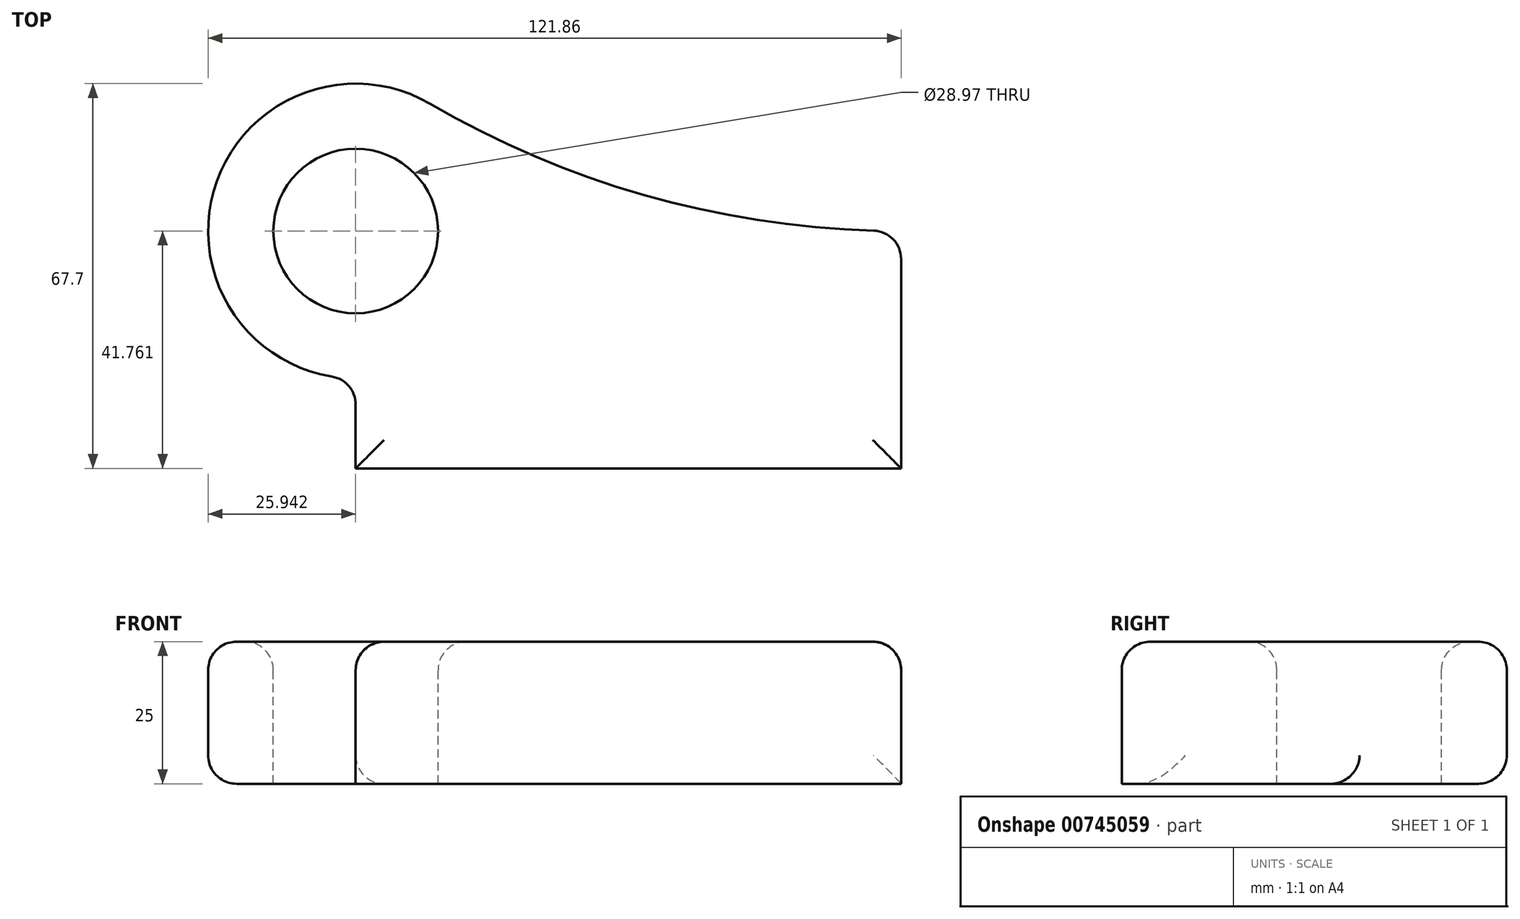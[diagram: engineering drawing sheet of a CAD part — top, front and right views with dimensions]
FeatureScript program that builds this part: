
annotation { "Feature Type Name" : "Feature", "Feature Type Description" : "" }
export const myFeature = defineFeature(function(context is Context, id is Id, definition is map)
    precondition{}
    {
        {
            var Q0;
            Q0=qCreatedBy(makeId("Top.planeOp"),FACE);
            var sketch = newSketch(context, id + "F0", { "sketchPlane" : qUnion([Q0])});
            skLineSegment(sketch, "E0.bottom", {"start": v(-47.96, -20.88) * mm, "end": v(47.96, -20.88) * mm});
            skLineSegment(sketch, "E0.top", {"start": v(-47.96, 20.88) * mm, "end": v(47.96, 20.88) * mm});
            skLineSegment(sketch, "E0.left", {"start": v(-47.96, -20.88) * mm, "end": v(-47.96, 20.88) * mm});
            skLineSegment(sketch, "E0.right", {"start": v(47.96, -20.88) * mm, "end": v(47.96, 20.88) * mm});
            skPoint(sketch, "E0.middle", {"position": v(0, 0) * mm});
            skCircle(sketch, "E1", {"center": v(-47.96, 20.88) * mm, "radius": 25.94 * mm});
            skArc(sketch, "E2", {"start": v(-34.88, 43.29) * mm, "mid": v(5.05, 26.58) * mm, "end": v(47.96, 20.88) * mm});
            skCircle(sketch, "E3", {"center": v(-47.96, 20.88) * mm, "radius": 14.48 * mm});
            skSolve(sketch);
        }
        {
            var Q0;
            {var subQ0=sQuery(id+"F0.wireOp",EDGE,"E2");Q0=makeQuery(id+"F0.imprint","IMPRINT",FACE,{"disambiguationData":[TD([[makeQuery(id+"F0.imprint","IMPRINT",EDGE,{"derivedFrom":subQ0}),-1.0]])]});}
            var Q1;
            {var subQ4=sQuery(id+"F0.wireOp",EDGE,"E0.top");var subQ6=sQuery(id+"F0.wireOp",EDGE,"E3");var subQ8=makeQuery(id+"F0.imprint","INTERSECT",VERTEX,{"derivedFrom":[subQ4,subQ6]});Q1=makeQuery(id+"F0.imprint","IMPRINT",FACE,{"disambiguationData":[TD([[makeQuery(id+"F0.imprint","IMPRINT",EDGE,{"disambiguationData":[TD([[subQ8,-1.0]])],"derivedFrom":subQ4}),1.0]])]});}
            var Q2;
            {var subQ0=sQuery(id+"F0.wireOp",EDGE,"E3");var subQ1=sQuery(id+"F0.wireOp",EDGE,"E0.top");var subQ2=makeQuery(id+"F0.imprint","INTERSECT",VERTEX,{"derivedFrom":[subQ1,subQ0]});Q2=makeQuery(id+"F0.imprint","IMPRINT",FACE,{"disambiguationData":[TD([[makeQuery(id+"F0.imprint","IMPRINT",EDGE,{"disambiguationData":[TD([[subQ2,-1.0]])],"derivedFrom":subQ1}),-1.0]])]});}
            var Q3;
            {var subQ2=sQuery(id+"F0.wireOp",EDGE,"E0.bottom");Q3=makeQuery(id+"F0.imprint","IMPRINT",FACE,{"disambiguationData":[TD([[makeQuery(id+"F0.imprint","IMPRINT",EDGE,{"derivedFrom":subQ2}),1.0]])]});}
            extrude(context, id + "F1", {"entities" : qUnion([Q0, Q1, Q2, Q3]), "oppositeDirection" : true, "depth" : 25 * mm, "offsetDistance" : 25 * mm});
        }
        {
            var Q0;
            Q0=sQuery(id+"F0.wireOp",EDGE,"E3");
            extrude(context, id + "F2", {"bodyType" : ToolBodyType.SURFACE, "surfaceEntities" : qUnion([Q0]), "endBound" : BoundingType.SYMMETRIC, "oppositeDirection" : true, "depth" : 286 * mm, "offsetDistance" : 25 * mm});
        }
        {
            var Q0;
            Q0=makeQuery(id+"F1.opExtrude","CAP_FACE",FACE,{"disambiguationData":[OSD([sQuery(id+"F0.wireOp",EDGE,"E0.bottom"),sQuery(id+"F0.wireOp",EDGE,"E0.left"),sQuery(id+"F0.wireOp",EDGE,"E0.right"),sQuery(id+"F0.wireOp",EDGE,"E1"),sQuery(id+"F0.wireOp",EDGE,"E2"),sQuery(id+"F0.wireOp",EDGE,"E3")])],"isStart":true});
            var Q1;
            Q1=makeQuery(id+"F1.opExtrude","SWEPT_FACE",FACE,{"disambiguationData":[OSD([sQuery(id+"F0.wireOp",EDGE,"E2")])]});
            var Q2;
            Q2=makeQuery(id+"F1.opExtrude","SWEPT_FACE",FACE,{"disambiguationData":[OSD([sQuery(id+"F0.wireOp",EDGE,"E1")])]});
            var Q3;
            Q3=makeQuery(id+"F2.opExtrude","SWEPT_FACE",FACE,{"disambiguationData":[OSD([sQuery(id+"F0.wireOp",EDGE,"E3")])]});
            fillet(context, id + "F3", {"entities" : qUnion([Q0, Q1, Q2, Q3]), "radius" : 5 * mm, "tangentPropagation" : true, "allowEdgeOverflow" : false});
        }
    });
